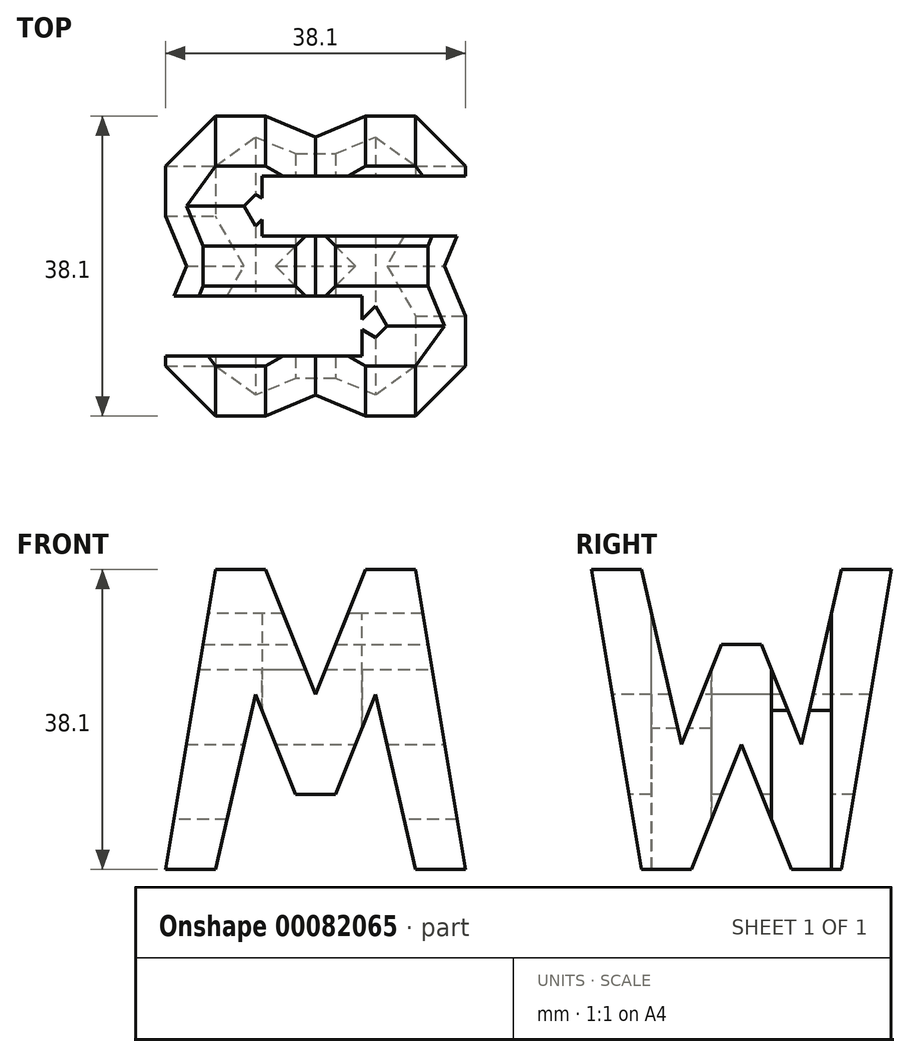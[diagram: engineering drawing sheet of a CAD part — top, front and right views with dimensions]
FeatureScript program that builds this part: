
annotation { "Feature Type Name" : "Feature", "Feature Type Description" : "" }
export const myFeature = defineFeature(function(context is Context, id is Id, definition is map)
    precondition{}
    {
        {
            var Q0;
            Q0=qCreatedBy(makeId("Front.planeOp"),FACE);
            var sketch = newSketch(context, id + "F0", { "sketchPlane" : qUnion([Q0])});
            skLineSegment(sketch, "E0", {"start": v(0, 0) * mm, "end": v(38.1, 0) * mm});
            skLineSegment(sketch, "E1", {"start": v(38.1, 0) * mm, "end": v(38.1, 38.1) * mm});
            skLineSegment(sketch, "E2", {"start": v(38.1, 38.1) * mm, "end": v(0, 38.1) * mm});
            skLineSegment(sketch, "E3", {"start": v(0, 38.1) * mm, "end": v(0, 0) * mm});
            skSolve(sketch);
        }
        {
            var Q0;
            Q0=makeQuery(id+"F0.imprint","IMPRINT",FACE,{"disambiguationData":[TD([[makeQuery(id+"F0.imprint","IMPRINT",EDGE,{"derivedFrom":sQuery(id+"F0.wireOp",EDGE,"E0")}),1.0]])]});
            extrude(context, id + "F1", {"entities" : qUnion([Q0]), "depth" : 38.1 * mm});
        }
        {
            var Q0;
            Q0=qCreatedBy(makeId("Front.planeOp"),FACE);
            cPlane(context, id + "F2", {"entities" : qUnion([Q0]), "cplaneType" : CPlaneType.OFFSET, "offset" : 38.1 * mm, "width" : 152.4 * mm, "height" : 152.4 * mm});
        }
        {
            var Q0;
            Q0=qCreatedBy(makeId("Right.planeOp"),FACE);
            cPlane(context, id + "F3", {"entities" : qUnion([Q0]), "cplaneType" : CPlaneType.OFFSET, "offset" : 38.1 * mm, "width" : 152.4 * mm, "height" : 152.4 * mm});
        }
        {
            var Q0;
            Q0=qCreatedBy(makeId("Top.planeOp"),FACE);
            cPlane(context, id + "F4", {"entities" : qUnion([Q0]), "cplaneType" : CPlaneType.OFFSET, "offset" : 38.1 * mm, "width" : 152.4 * mm, "height" : 152.4 * mm});
        }
        {
            var Q0;
            Q0=qCreatedBy(id+"F3.planeOp",FACE);
            var sketch = newSketch(context, id + "F5", { "sketchPlane" : qUnion([Q0])});
            skLineSegment(sketch, "E4", {"start": v(0, 0) * mm, "end": v(0, 38.1) * mm});
            skLineSegment(sketch, "E5", {"start": v(0, 38.1) * mm, "end": v(-38.1, 38.1) * mm});
            skLineSegment(sketch, "E6", {"start": v(-38.1, 38.1) * mm, "end": v(-38.1, 0) * mm});
            skLineSegment(sketch, "E7", {"start": v(-38.1, 0) * mm, "end": v(0, 0) * mm});
            skSolve(sketch);
        }
        {
            var Q0;
            Q0=makeQuery(id+"F5.imprint","IMPRINT",FACE,{"disambiguationData":[TD([[makeQuery(id+"F5.imprint","IMPRINT",EDGE,{"derivedFrom":sQuery(id+"F5.wireOp",EDGE,"E4")}),1.0]])]});
            extrude(context, id + "F6", {"entities" : qUnion([Q0]), "operationType" : NewBodyOperationType.ADD, "depth" : 38.1 * mm});
        }
        {
            var Q0;
            Q0=makeQuery(id+"F6.opExtrude","CAP_FACE",FACE,{"disambiguationData":[OSD([sQuery(id+"F5.wireOp",EDGE,"E4"),sQuery(id+"F5.wireOp",EDGE,"E5"),sQuery(id+"F5.wireOp",EDGE,"E6"),sQuery(id+"F5.wireOp",EDGE,"E7")])],"isStart":false});
            var sketch = newSketch(context, id + "F7", { "sketchPlane" : qUnion([Q0])});
            skLineSegment(sketch, "E8", {"start": v(-38.1, 38.1) * mm, "end": v(-31.75, 0) * mm});
            skLineSegment(sketch, "E9", {"start": v(-25.4, 0) * mm, "end": v(-19.05, 15.88) * mm});
            skLineSegment(sketch, "E10", {"start": v(-19.05, 15.88) * mm, "end": v(-12.7, 0) * mm});
            skLineSegment(sketch, "E11", {"start": v(-6.35, 0) * mm, "end": v(0, 38.1) * mm});
            skLineSegment(sketch, "E12", {"start": v(-6.35, 38.1) * mm, "end": v(-11.43, 15.87) * mm});
            skLineSegment(sketch, "E13", {"start": v(-11.43, 15.87) * mm, "end": v(-16.51, 28.57) * mm});
            skLineSegment(sketch, "E14", {"start": v(-16.5, 28.57) * mm, "end": v(-21.59, 28.57) * mm});
            skLineSegment(sketch, "E15", {"start": v(-21.6, 28.58) * mm, "end": v(-26.67, 15.87) * mm});
            skLineSegment(sketch, "E16", {"start": v(-26.67, 15.87) * mm, "end": v(-31.75, 38.1) * mm});
            skLineSegment(sketch, "E17", {"start": v(-38.1, 38.1) * mm, "end": v(-31.75, 38.1) * mm});
            skLineSegment(sketch, "E18", {"start": v(-6.35, 38.1) * mm, "end": v(0, 38.1) * mm});
            skLineSegment(sketch, "E19", {"start": v(-6.35, 0) * mm, "end": v(-12.7, 0) * mm});
            skLineSegment(sketch, "E20", {"start": v(-25.4, 0) * mm, "end": v(-31.75, 0) * mm});
            skSolve(sketch);
        }
        {
            var Q0;
            Q0=makeQuery(id+"F1.opExtrude","SWEPT_FACE",FACE,{"disambiguationData":[OSD([sQuery(id+"F0.wireOp",EDGE,"E3")])]});
            extrude(context, id + "F8", {"entities" : qUnion([Q0]), "operationType" : NewBodyOperationType.REMOVE, "oppositeDirection" : true, "depth" : 38.1 * mm});
        }
        {
            var Q0;
            {var subQ0=sQuery(id+"F7.wireOp",EDGE,"E12");Q0=makeQuery(id+"F7.imprint","IMPRINT",FACE,{"disambiguationData":[TD([[makeQuery(id+"F7.imprint","IMPRINT",EDGE,{"derivedFrom":subQ0}),-1.0]])]});}
            var Q1;
            {var subQ0=sQuery(id+"F7.wireOp",EDGE,"E9");Q1=makeQuery(id+"F7.imprint","IMPRINT",FACE,{"disambiguationData":[TD([[makeQuery(id+"F7.imprint","IMPRINT",EDGE,{"derivedFrom":subQ0}),-1.0]])]});}
            var Q2;
            {var subQ0=sQuery(id+"F7.wireOp",EDGE,"E11");Q2=makeQuery(id+"F7.imprint","IMPRINT",FACE,{"disambiguationData":[TD([[makeQuery(id+"F7.imprint","IMPRINT",EDGE,{"derivedFrom":subQ0}),-1.0]])]});}
            var Q3;
            {var subQ0=sQuery(id+"F7.wireOp",EDGE,"E8");Q3=makeQuery(id+"F7.imprint","IMPRINT",FACE,{"disambiguationData":[TD([[makeQuery(id+"F7.imprint","IMPRINT",EDGE,{"derivedFrom":subQ0}),-1.0]])]});}
            extrude(context, id + "F9", {"entities" : qUnion([Q0, Q1, Q2, Q3]), "operationType" : NewBodyOperationType.REMOVE, "oppositeDirection" : true, "depth" : 38.1 * mm});
        }
        {
            var Q0;
            Q0=qCreatedBy(id+"F2.planeOp",FACE);
            var sketch = newSketch(context, id + "F10", { "sketchPlane" : qUnion([Q0])});
            skLineSegment(sketch, "E21", {"start": v(38.1, 0) * mm, "end": v(44.45, 38.1) * mm});
            skLineSegment(sketch, "E22", {"start": v(44.45, 38.1) * mm, "end": v(50.8, 38.1) * mm});
            skLineSegment(sketch, "E23", {"start": v(50.8, 38.1) * mm, "end": v(57.15, 22.23) * mm});
            skLineSegment(sketch, "E24", {"start": v(57.15, 22.23) * mm, "end": v(63.5, 38.1) * mm});
            skLineSegment(sketch, "E25", {"start": v(63.5, 38.1) * mm, "end": v(69.85, 38.1) * mm});
            skLineSegment(sketch, "E26", {"start": v(69.85, 38.1) * mm, "end": v(76.2, 0) * mm});
            skLineSegment(sketch, "E27", {"start": v(76.2, 0) * mm, "end": v(69.85, 0) * mm});
            skLineSegment(sketch, "E28", {"start": v(69.85, 0) * mm, "end": v(64.77, 22.22) * mm});
            skLineSegment(sketch, "E29", {"start": v(64.77, 22.23) * mm, "end": v(59.69, 9.52) * mm});
            skLineSegment(sketch, "E30", {"start": v(59.7, 9.53) * mm, "end": v(54.61, 9.53) * mm});
            skLineSegment(sketch, "E31", {"start": v(54.61, 9.53) * mm, "end": v(49.53, 22.23) * mm});
            skLineSegment(sketch, "E32", {"start": v(49.53, 22.23) * mm, "end": v(44.45, 0) * mm});
            skLineSegment(sketch, "E33", {"start": v(44.45, 0) * mm, "end": v(38.1, 0) * mm});
            skLineSegment(sketch, "E34.bottom", {"start": v(38.1, 0) * mm, "end": v(76.2, 0) * mm});
            skLineSegment(sketch, "E34.top", {"start": v(38.1, 38.1) * mm, "end": v(76.2, 38.1) * mm});
            skLineSegment(sketch, "E34.left", {"start": v(38.1, 0) * mm, "end": v(38.1, 38.1) * mm});
            skLineSegment(sketch, "E34.right", {"start": v(76.2, 0) * mm, "end": v(76.2, 38.1) * mm});
            skSolve(sketch);
        }
        {
            var Q0;
            {var subQ0=sQuery(id+"F10.wireOp",EDGE,"E23");Q0=makeQuery(id+"F10.imprint","IMPRINT",FACE,{"disambiguationData":[TD([[makeQuery(id+"F10.imprint","IMPRINT",EDGE,{"derivedFrom":subQ0}),1.0]])]});}
            var Q1;
            {var subQ0=sQuery(id+"F10.wireOp",EDGE,"E28");Q1=makeQuery(id+"F10.imprint","IMPRINT",FACE,{"disambiguationData":[TD([[makeQuery(id+"F10.imprint","IMPRINT",EDGE,{"derivedFrom":subQ0}),1.0]])]});}
            var Q2;
            {var subQ0=sQuery(id+"F10.wireOp",EDGE,"E26");Q2=makeQuery(id+"F10.imprint","IMPRINT",FACE,{"disambiguationData":[TD([[makeQuery(id+"F10.imprint","IMPRINT",EDGE,{"derivedFrom":subQ0}),1.0]])]});}
            var Q3;
            {var subQ0=sQuery(id+"F10.wireOp",EDGE,"E21");Q3=makeQuery(id+"F10.imprint","IMPRINT",FACE,{"disambiguationData":[TD([[makeQuery(id+"F10.imprint","IMPRINT",EDGE,{"derivedFrom":subQ0}),1.0]])]});}
            extrude(context, id + "F11", {"entities" : qUnion([Q0, Q1, Q2, Q3]), "operationType" : NewBodyOperationType.REMOVE, "oppositeDirection" : true, "depth" : 38.1 * mm});
        }
        {
            var Q0;
            Q0=qCreatedBy(id+"F4.planeOp",FACE);
            var sketch = newSketch(context, id + "F12", { "sketchPlane" : qUnion([Q0])});
            skLineSegment(sketch, "E35.bottom", {"start": v(37.64, 0) * mm, "end": v(75.74, 0) * mm});
            skLineSegment(sketch, "E35.top", {"start": v(37.64, -38.1) * mm, "end": v(75.74, -38.1) * mm});
            skLineSegment(sketch, "E35.left", {"start": v(37.64, 0) * mm, "end": v(37.64, -38.1) * mm});
            skLineSegment(sketch, "E35.right", {"start": v(75.74, 0) * mm, "end": v(75.74, -38.1) * mm});
            skSolve(sketch);
        }
        {
            var Q0;
            Q0=makeQuery(id+"F12.imprint","IMPRINT",FACE,{"disambiguationData":[TD([[makeQuery(id+"F12.imprint","IMPRINT",EDGE,{"derivedFrom":sQuery(id+"F12.wireOp",EDGE,"E35.bottom")}),-1.0]])]});
            var sketch = newSketch(context, id + "F13", { "sketchPlane" : qUnion([Q0])});
            skLineSegment(sketch, "E36", {"start": v(50.34, -7.62) * mm, "end": v(50.34, -15.24) * mm});
            skLineSegment(sketch, "E37", {"start": v(50.34, -15.24) * mm, "end": v(79.31, -15.24) * mm});
            skLineSegment(sketch, "E38", {"start": v(79.31, -15.24) * mm, "end": v(79.31, -7.62) * mm});
            skLineSegment(sketch, "E39", {"start": v(79.31, -7.62) * mm, "end": v(50.34, -7.62) * mm});
            skLineSegment(sketch, "E40", {"start": v(63.04, -22.05) * mm, "end": v(63.04, -30.48) * mm});
            skLineSegment(sketch, "E41", {"start": v(63.04, -30.48) * mm, "end": v(31.54, -30.48) * mm});
            skLineSegment(sketch, "E42", {"start": v(31.54, -30.48) * mm, "end": v(31.54, -22.86) * mm});
            skLineSegment(sketch, "E43", {"start": v(31.54, -22.86) * mm, "end": v(64.8, -22.86) * mm});
            skSolve(sketch);
        }
        {
            var Q0;
            Q0 = qSketchRegion(id + "F13", true);
            extrude(context, id + "F14", {"entities" : qUnion([Q0]), "operationType" : NewBodyOperationType.REMOVE, "oppositeDirection" : true, "depth" : 38.1 * mm});
        }
    });
